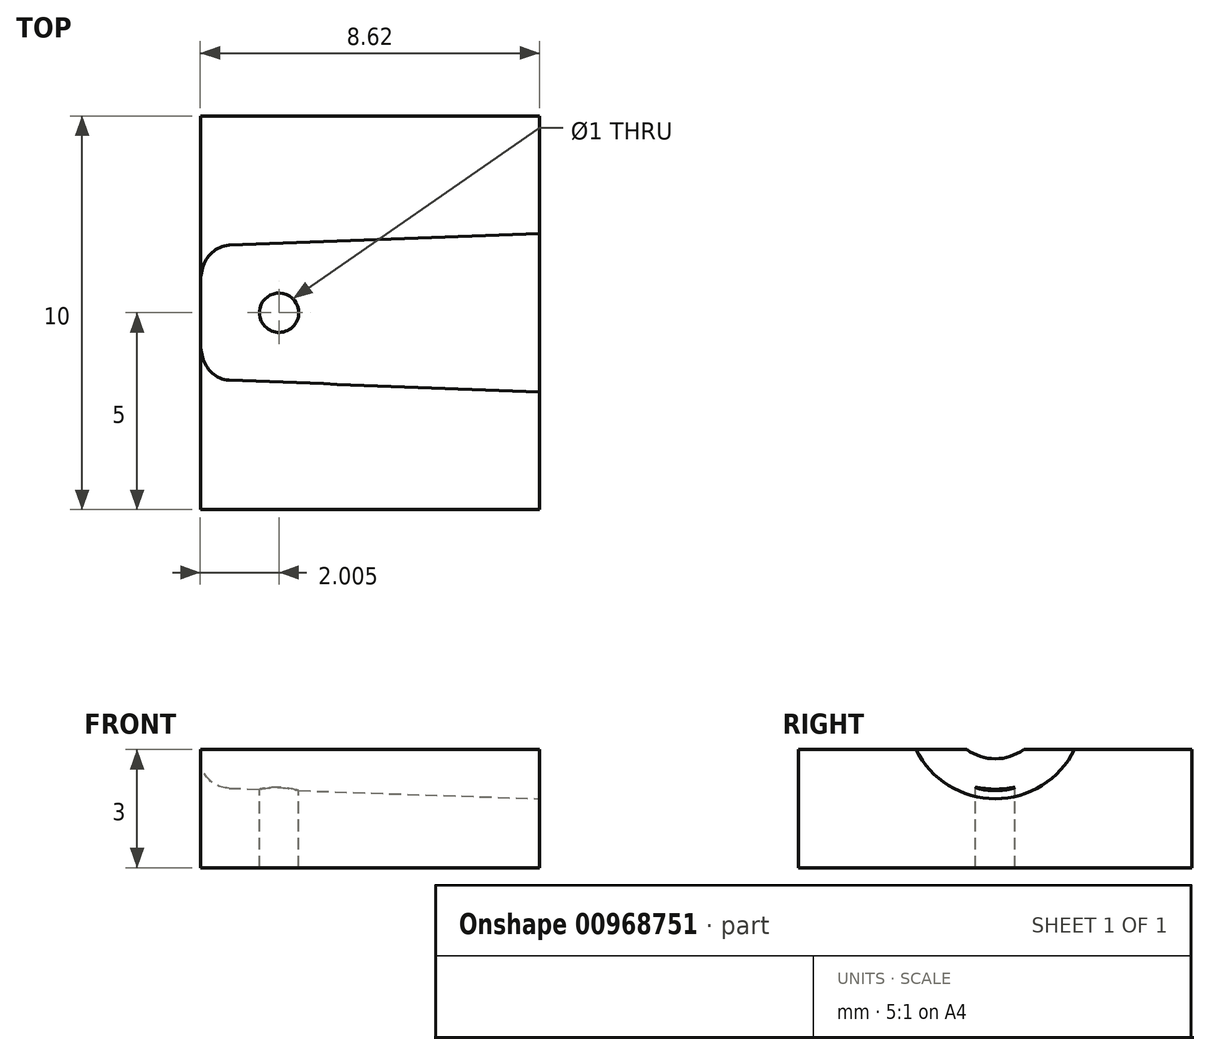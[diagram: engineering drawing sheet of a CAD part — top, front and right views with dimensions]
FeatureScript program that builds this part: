
annotation { "Feature Type Name" : "Feature", "Feature Type Description" : "" }
export const myFeature = defineFeature(function(context is Context, id is Id, definition is map)
    precondition{}
    {
        {
            var Q0;
            Q0=qCreatedBy(makeId("Top.planeOp"),FACE);
            var sketch = newSketch(context, id + "F0", { "sketchPlane" : qUnion([Q0])});
            skLineSegment(sketch, "E0.bottom", {"start": v(4.3, 5) * mm, "end": v(-4.3, 5) * mm});
            skLineSegment(sketch, "E0.top", {"start": v(4.3, -5) * mm, "end": v(-4.3, -5) * mm});
            skLineSegment(sketch, "E0.left", {"start": v(4.3, 5) * mm, "end": v(4.3, -5) * mm});
            skLineSegment(sketch, "E0.right", {"start": v(-4.3, 5) * mm, "end": v(-4.3, -5) * mm});
            skPoint(sketch, "E0.middle", {"position": v(0, 0) * mm});
            skSolve(sketch);
        }
        {
            var Q0;
            Q0 = qSketchRegion(id + "F0", true);
            extrude(context, id + "F1", {"entities" : qUnion([Q0]), "oppositeDirection" : true, "depth" : 3 * mm, "offsetDistance" : 25 * mm});
        }
        {
            var Q0;
            Q0=qCreatedBy(makeId("Front.planeOp"),FACE);
            var sketch = newSketch(context, id + "F2", { "sketchPlane" : qUnion([Q0])});
            skLineSegment(sketch, "E1", {"start": v(-3.58, -0.98) * mm, "end": v(4.3, -1.25) * mm});
            skLineSegment(sketch, "E2", {"start": v(4.3, -1.25) * mm, "end": v(4.3, 1) * mm});
            skLineSegment(sketch, "E3", {"start": v(4.3, 1) * mm, "end": v(-4.3, 1) * mm});
            skLineSegment(sketch, "E4", {"start": v(-4.3, 1) * mm, "end": v(-4.3, -0.23) * mm});
            skArc(sketch, "E5", {"start": v(-4.3, -0.23) * mm, "mid": v(-4.1, -0.75) * mm, "end": v(-3.58, -0.98) * mm});
            skSolve(sketch);
        }
        {
            var Q0;
            Q0 = qSketchRegion(id + "F2", true);
            var Q1;
            Q1=sQuery(id+"F2.wireOp",EDGE,"E3");
            revolve(context, id + "F3", {"operationType" : NewBodyOperationType.REMOVE, "surfaceOperationType" : NewSurfaceOperationType.NEW, "entities" : qUnion([Q0]), "axis" : qUnion([Q1]), "revolveType" : RevolveType.FULL, "oppositeDirection" : true});
        }
        {
            var Q0;
            {var subQ0=sQuery(id+"F0.wireOp",EDGE,"E0.left");var subQ1=sQuery(id+"F0.wireOp",EDGE,"E0.right");var subQ2=sQuery(id+"F0.wireOp",EDGE,"E0.bottom");Q0=makeQuery(id+"F3.boolean.opBoolean","SPLIT",FACE,{"disambiguationData":[TD([makeQuery(id+"F1.opExtrude","SWEPT_FACE",FACE,{"disambiguationData":[OSD([subQ2])]})])],"derivedFrom":makeQuery(id+"F1.opExtrude","CAP_FACE",FACE,{"disambiguationData":[OSD([subQ2,sQuery(id+"F0.wireOp",EDGE,"E0.top"),subQ0,subQ1])],"isStart":true})});}
            var sketch = newSketch(context, id + "F4", { "sketchPlane" : qUnion([Q0])});
            skCircle(sketch, "E6", {"center": v(-2.3, 0) * mm, "radius": 0.5 * mm});
            skSolve(sketch);
        }
        {
            var Q0;
            Q0 = qSketchRegion(id + "F4", true);
            extrude(context, id + "F5", {"entities" : qUnion([Q0]), "operationType" : NewBodyOperationType.REMOVE, "oppositeDirection" : true, "depth" : 25 * mm, "offsetDistance" : 25 * mm});
        }
    });
